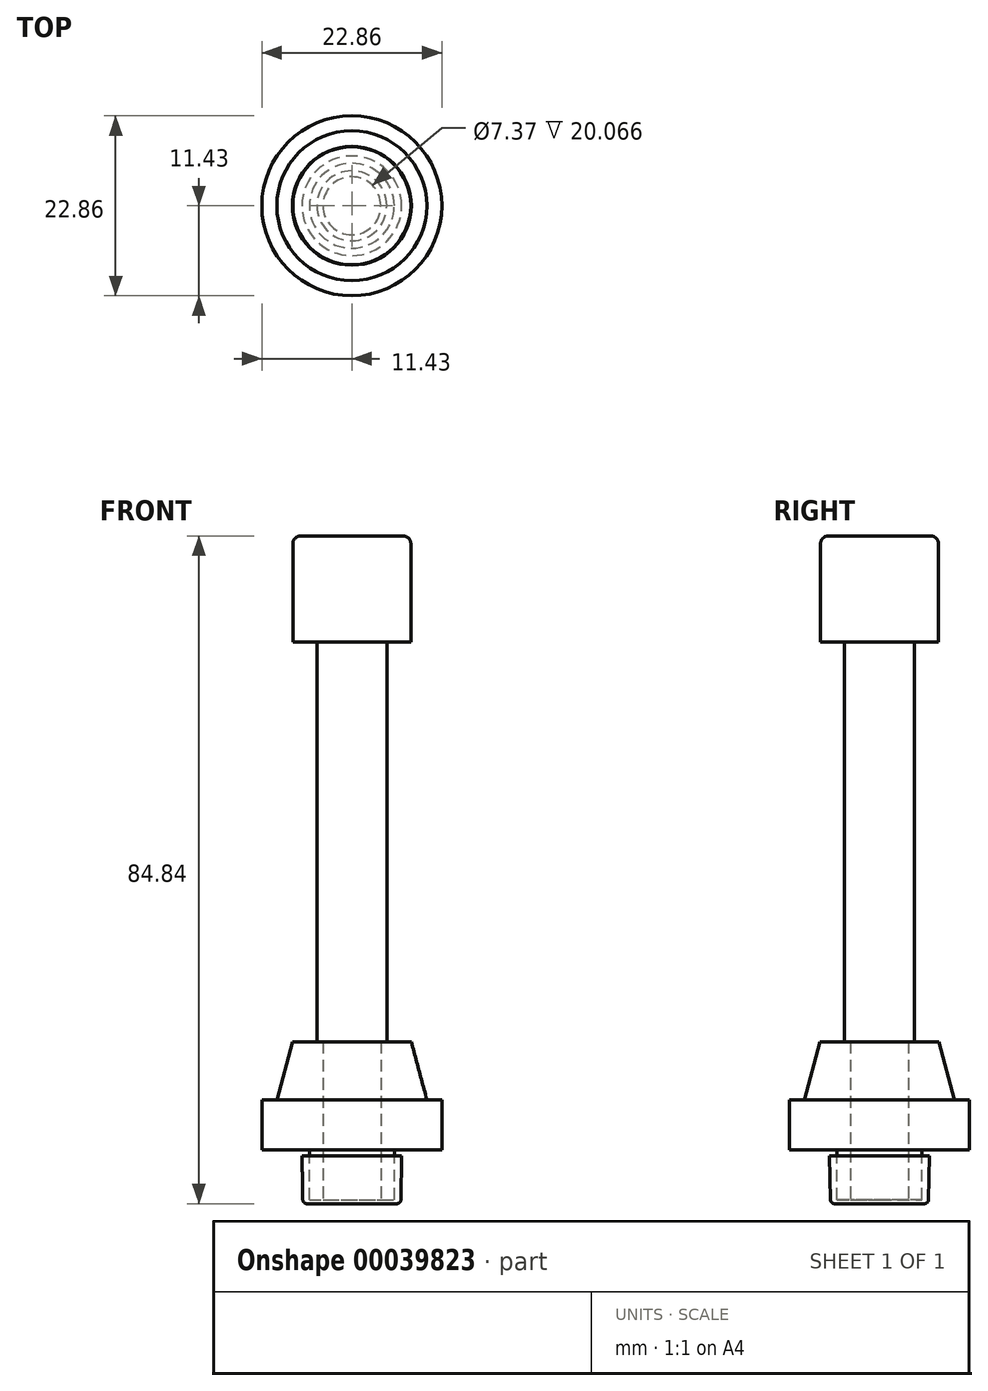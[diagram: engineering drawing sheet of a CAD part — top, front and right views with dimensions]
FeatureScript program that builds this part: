
annotation { "Feature Type Name" : "Feature", "Feature Type Description" : "" }
export const myFeature = defineFeature(function(context is Context, id is Id, definition is map)
    precondition{}
    {
        {
            var Q0;
            Q0=qCreatedBy(makeId("Top.planeOp"),FACE);
            var sketch = newSketch(context, id + "F0", { "sketchPlane" : qUnion([Q0])});
            skCircle(sketch, "E0", {"center": v(0, 0) * mm, "radius": 11.43 * mm});
            skSolve(sketch);
        }
        {
            var Q0;
            Q0 = qSketchRegion(id + "F0", true);
            extrude(context, id + "F1", {"entities" : qUnion([Q0]), "depth" : 6.35 * mm});
        }
        {
            var Q0;
            Q0=makeQuery(id+"F1.opExtrude","CAP_FACE",FACE,{"disambiguationData":[OSD([sQuery(id+"F0.wireOp",EDGE,"E0")])],"isStart":false});
            var sketch = newSketch(context, id + "F2", { "sketchPlane" : qUnion([Q0])});
            skCircle(sketch, "E1", {"center": v(0, 0) * mm, "radius": 9.53 * mm});
            skSolve(sketch);
        }
        {
            var Q0;
            Q0 = qSketchRegion(id + "F2", true);
            extrude(context, id + "F3", {"entities" : qUnion([Q0]), "operationType" : NewBodyOperationType.ADD, "depth" : 7.37 * mm, "hasDraft" : true, "draftAngle" : 15 * degree, "draftPullDirection" : true});
        }
        {
            var Q0;
            Q0=makeQuery(id+"F1.opExtrude","CAP_FACE",FACE,{"disambiguationData":[OSD([sQuery(id+"F0.wireOp",EDGE,"E0")])],"isStart":true});
            var sketch = newSketch(context, id + "F4", { "sketchPlane" : qUnion([Q0])});
            skCircle(sketch, "E2", {"center": v(0, 0) * mm, "radius": 5.4 * mm});
            skSolve(sketch);
        }
        {
            var Q0;
            Q0 = qSketchRegion(id + "F4", true);
            extrude(context, id + "F5", {"entities" : qUnion([Q0]), "operationType" : NewBodyOperationType.ADD, "depth" : 6.35 * mm});
        }
        {
            var Q0;
            Q0=makeQuery(id+"F5.opExtrude","CAP_FACE",FACE,{"disambiguationData":[OSD([sQuery(id+"F4.wireOp",EDGE,"E2")])],"isStart":false});
            var sketch = newSketch(context, id + "F6", { "sketchPlane" : qUnion([Q0])});
            skCircle(sketch, "E3", {"center": v(0, 0) * mm, "radius": 3.68 * mm});
            skSolve(sketch);
        }
        {
            var Q0;
            Q0 = qSketchRegion(id + "F6", true);
            extrude(context, id + "F7", {"entities" : qUnion([Q0]), "operationType" : NewBodyOperationType.REMOVE, "endBound" : BoundingType.THROUGH_ALL, "oppositeDirection" : true, "depth" : 25.4 * mm});
        }
        {
            var Q0;
            Q0=makeQuery(id+"F3.opExtrude","CAP_FACE",FACE,{"disambiguationData":[OSD([sQuery(id+"F2.wireOp",EDGE,"E1")])],"isStart":false});
            var sketch = newSketch(context, id + "F8", { "sketchPlane" : qUnion([Q0])});
            skCircle(sketch, "E4", {"center": v(0, 0) * mm, "radius": 4.45 * mm});
            skSolve(sketch);
        }
        {
            var Q0;
            Q0 = qSketchRegion(id + "F8", true);
            extrude(context, id + "F9", {"entities" : qUnion([Q0]), "depth" : 50.8 * mm});
        }
        {
            var Q0;
            Q0=makeQuery(id+"F9.opExtrude","CAP_FACE",FACE,{"disambiguationData":[OSD([sQuery(id+"F8.wireOp",EDGE,"E4")])],"isStart":false});
            var sketch = newSketch(context, id + "F10", { "sketchPlane" : qUnion([Q0])});
            skCircle(sketch, "E5", {"center": v(0, 0) * mm, "radius": 7.5 * mm});
            skSolve(sketch);
        }
        {
            var Q0;
            Q0 = qSketchRegion(id + "F10", true);
            extrude(context, id + "F11", {"entities" : qUnion([Q0]), "depth" : 13.46 * mm});
        }
        {
            var Q0;
            Q0=makeQuery(id+"F11.opExtrude","CAP_EDGE",EDGE,{"disambiguationData":[OSD([sQuery(id+"F10.wireOp",EDGE,"E5")])],"isStart":false});
            fillet(context, id + "F12", {"entities" : qUnion([Q0]), "radius" : 1.02 * mm, "tangentPropagation" : true, "allowEdgeOverflow" : false});
        }
        {
            var Q0;
            Q0=makeQuery(id+"F5.opExtrude","CAP_FACE",FACE,{"disambiguationData":[OSD([sQuery(id+"F4.wireOp",EDGE,"E2")])],"isStart":false});
            cPlane(context, id + "F13", {"entities" : qUnion([Q0]), "cplaneType" : CPlaneType.OFFSET, "offset" : 0.5 * mm, "width" : 152.4 * mm, "height" : 152.4 * mm});
        }
        {
            var Q0;
            Q0=qCreatedBy(id+"F13.planeOp",FACE);
            var sketch = newSketch(context, id + "F14", { "sketchPlane" : qUnion([Q0])});
            skCircle(sketch, "E6", {"center": v(0, 0) * mm, "radius": 6.22 * mm});
            skSolve(sketch);
        }
        {
            var Q0;
            Q0 = qSketchRegion(id + "F14", true);
            extrude(context, id + "F15", {"entities" : qUnion([Q0]), "oppositeDirection" : true, "depth" : 6.1 * mm, "hasDraft" : true, "draftAngle" : 1 * degree});
        }
        {
            var Q0;
            Q0=makeQuery(id+"F15.opExtrude","CAP_EDGE",EDGE,{"disambiguationData":[OSD([sQuery(id+"F14.wireOp",EDGE,"E6")])],"isStart":true});
            fillet(context, id + "F16", {"entities" : qUnion([Q0]), "radius" : 0.5 * mm, "tangentPropagation" : true, "allowEdgeOverflow" : false});
        }
    });
